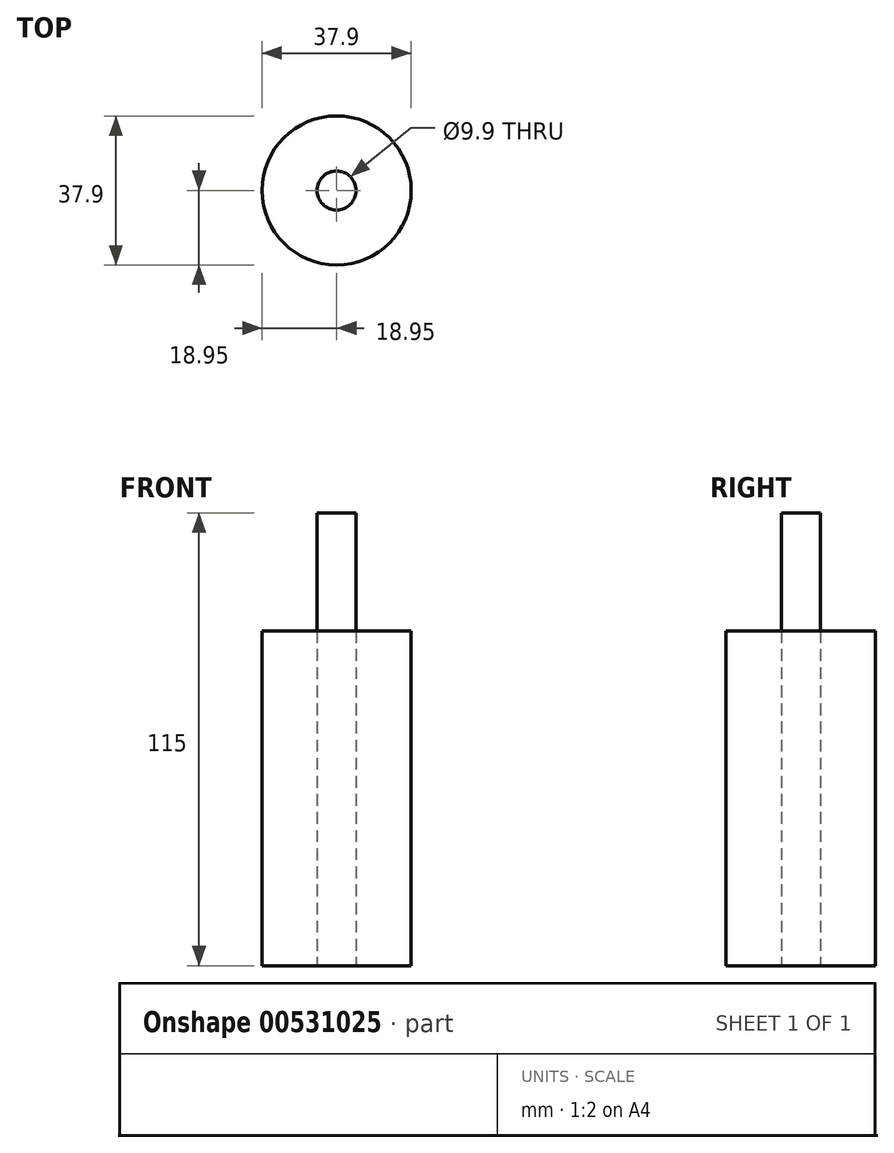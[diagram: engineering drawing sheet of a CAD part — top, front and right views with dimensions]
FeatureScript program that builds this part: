
annotation { "Feature Type Name" : "Feature", "Feature Type Description" : "" }
export const myFeature = defineFeature(function(context is Context, id is Id, definition is map)
    precondition{}
    {
        {
            var Q0;
            Q0=qCreatedBy(makeId("Top.planeOp"),FACE);
            var sketch = newSketch(context, id + "F0", { "sketchPlane" : qUnion([Q0])});
            skCircle(sketch, "E0", {"center": v(0, 0) * mm, "radius": 18.95 * mm});
            skSolve(sketch);
        }
        {
            var Q0;
            Q0=makeQuery(id+"F0.imprint","IMPRINT",FACE,{"disambiguationData":[TD([[makeQuery(id+"F0.imprint","IMPRINT",EDGE,{"derivedFrom":sQuery(id+"F0.wireOp",EDGE,"E0")}),1.0]])]});
            extrude(context, id + "F1", {"entities" : qUnion([Q0]), "endBound" : BoundingType.SYMMETRIC, "depth" : 85 * mm, "offsetDistance" : 25 * mm});
        }
        {
            var Q0;
            Q0=makeQuery(id+"F1.opExtrude","CAP_FACE",FACE,{"disambiguationData":[OSD([sQuery(id+"F0.wireOp",EDGE,"E0")])],"isStart":true});
            var sketch = newSketch(context, id + "F2", { "sketchPlane" : qUnion([Q0])});
            skPoint(sketch, "E1", {"position": v(0, 16.25) * mm});
            skSolve(sketch);
        }
        {
            var Q0;
            Q0=sQuery(id+"F2.wireOp",VERTEX,"E1");
            var Q1;
            Q1=qCreatedBy(makeId("Front.planeOp"),FACE);
            cPlane(context, id + "F3", {"entities" : qUnion([Q0, Q1]), "cplaneType" : CPlaneType.PLANE_POINT, "offset" : 25 * mm, "width" : 150 * mm, "height" : 150 * mm});
        }
        {
            var Q0;
            Q0=makeQuery(id+"F2.imprint","IMPRINT",FACE,{"disambiguationData":[TD([[makeQuery(id+"F2.imprint","IMPRINT",EDGE,{"derivedFrom":makeQuery(id+"F1.opExtrude","CAP_EDGE",EDGE,{"disambiguationData":[OSD([sQuery(id+"F0.wireOp",EDGE,"E0")])],"isStart":true})}),-1.0]])]});
            var sketch = newSketch(context, id + "F4", { "sketchPlane" : qUnion([Q0])});
            skCircle(sketch, "E2", {"center": v(0, 0) * mm, "radius": 4.95 * mm});
            skSolve(sketch);
        }
        {
            var Q0;
            Q0 = qSketchRegion(id + "F4", true);
            extrude(context, id + "F5", {"entities" : qUnion([Q0]), "operationType" : NewBodyOperationType.REMOVE, "endBound" : BoundingType.UP_TO_NEXT, "oppositeDirection" : true, "depth" : 25 * mm, "offsetDistance" : 25 * mm});
        }
        {
            var Q0;
            Q0=makeQuery(id+"F2.imprint","IMPRINT",FACE,{"disambiguationData":[TD([[makeQuery(id+"F2.imprint","IMPRINT",EDGE,{"derivedFrom":makeQuery(id+"F1.opExtrude","CAP_EDGE",EDGE,{"disambiguationData":[OSD([sQuery(id+"F0.wireOp",EDGE,"E0")])],"isStart":true})}),-1.0]])]});
            var sketch = newSketch(context, id + "F6", { "sketchPlane" : qUnion([Q0])});
            skCircle(sketch, "E3.0", {"center": v(0, 0) * mm, "radius": 4.95 * mm});
            skSolve(sketch);
        }
        {
            var Q0;
            Q0 = qSketchRegion(id + "F6", true);
            extrude(context, id + "F7", {"entities" : qUnion([Q0]), "oppositeDirection" : true, "depth" : 115 * mm, "offsetDistance" : 25 * mm});
        }
    });
